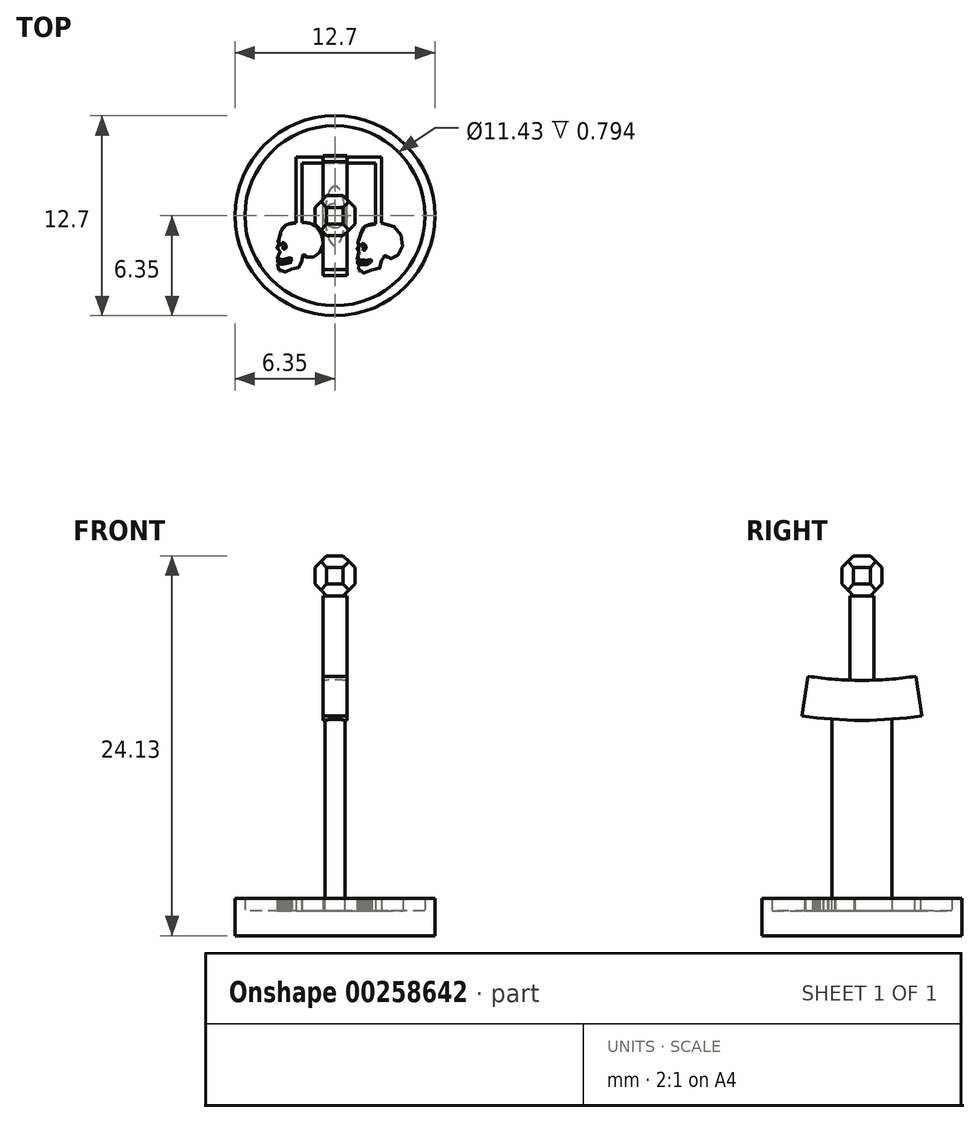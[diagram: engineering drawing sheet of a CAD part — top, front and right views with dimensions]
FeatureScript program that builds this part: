
annotation { "Feature Type Name" : "Feature", "Feature Type Description" : "" }
export const myFeature = defineFeature(function(context is Context, id is Id, definition is map)
    precondition{}
    {
        {
            var Q0;
            Q0=qCreatedBy(makeId("Top.planeOp"),FACE);
            var sketch = newSketch(context, id + "F0", { "sketchPlane" : qUnion([Q0])});
            skCircle(sketch, "E0", {"center": v(0, 0) * mm, "radius": 6.35 * mm});
            skSolve(sketch);
        }
        {
            var Q0;
            Q0 = qSketchRegion(id + "F0", true);
            extrude(context, id + "F1", {"entities" : qUnion([Q0]), "depth" : 1.59 * mm});
        }
        {
            var Q0;
            Q0=makeQuery(id+"F1.opExtrude","CAP_FACE",FACE,{"disambiguationData":[OSD([sQuery(id+"F0.wireOp",EDGE,"E0")])],"isStart":false});
            var sketch = newSketch(context, id + "F2", { "sketchPlane" : qUnion([Q0])});
            skCircle(sketch, "E1", {"center": v(0, 0) * mm, "radius": 5.72 * mm});
            skCircle(sketch, "E2.0", {"center": v(0, 0) * mm, "radius": 6.35 * mm});
            skFitSpline(sketch, "E3", {"points": [v(-2.99, -3.48) * mm, v(-2.95, -3.46) * mm, v(-2.86, -3.42) * mm, v(-2.74, -3.39) * mm, v(-2.6, -3.35) * mm, v(-2.43, -3.3) * mm, v(-2.3, -3.28) * mm, v(-2.2, -3.25) * mm, v(-2.15, -3.14) * mm, v(-2.13, -3.01) * mm, v(-2.13, -2.82) * mm, v(-2.12, -2.72) * mm, v(-2.07, -2.57) * mm, v(-2, -2.44) * mm, v(-1.95, -2.43) * mm, v(-1.87, -2.47) * mm, v(-1.8, -2.57) * mm, v(-1.76, -2.65) * mm, v(-1.67, -2.67) * mm, v(-1.54, -2.67) * mm, v(-1.4, -2.63) * mm, v(-1.28, -2.57) * mm, v(-1.17, -2.5) * mm, v(-1.04, -2.4) * mm, v(-0.91, -2.23) * mm, v(-0.83, -2.05) * mm, v(-0.77, -1.87) * mm, v(-0.77, -1.6) * mm, v(-0.82, -1.35) * mm, v(-0.9, -1.14) * mm, v(-1.03, -0.9) * mm, v(-1.19, -0.72) * mm, v(-1.49, -0.53) * mm, v(-1.79, -0.45) * mm, v(-2.09, -0.45) * mm, v(-2.47, -0.46) * mm, v(-2.74, -0.46) * mm, v(-2.94, -0.5) * mm, v(-3.18, -0.62) * mm, v(-3.33, -0.78) * mm, v(-3.4, -0.96) * mm, v(-3.45, -1.13) * mm, v(-3.45, -1.23) * mm, v(-3.5, -1.37) * mm, v(-3.57, -1.5) * mm, v(-3.61, -1.59) * mm, v(-3.6, -1.65) * mm, v(-3.56, -1.72) * mm, v(-3.53, -1.77) * mm, v(-3.51, -1.85) * mm, v(-3.57, -1.93) * mm, v(-3.6, -1.96) * mm, v(-3.66, -2) * mm, v(-3.66, -2.01) * mm, v(-3.67, -2.03) * mm, v(-3.66, -2.05) * mm, v(-3.65, -2.07) * mm, v(-3.63, -2.09) * mm, v(-3.53, -2.23) * mm, v(-3.46, -2.33) * mm, v(-3.48, -2.4) * mm, v(-3.54, -2.44) * mm, v(-3.6, -2.48) * mm, v(-3.61, -2.49) * mm, v(-3.6, -2.5) * mm, v(-3.57, -2.52) * mm, v(-3.56, -2.54) * mm, v(-3.57, -2.57) * mm, v(-3.6, -2.6) * mm, v(-3.65, -2.66) * mm, v(-3.66, -2.72) * mm, v(-3.59, -2.76) * mm, v(-3.44, -2.8) * mm, v(-3.3, -2.78) * mm, v(-3.16, -2.74) * mm, v(-3.02, -2.7) * mm, v(-2.86, -2.69) * mm, v(-2.77, -2.7) * mm, v(-2.74, -2.74) * mm, v(-2.73, -2.81) * mm, v(-2.74, -2.88) * mm, v(-2.78, -2.96) * mm, v(-2.92, -3) * mm, v(-3, -3.03) * mm, v(-3.1, -3.05) * mm, v(-3.29, -3.07) * mm, v(-3.43, -3.07) * mm, v(-3.55, -3.04) * mm, v(-3.62, -3.03) * mm, v(-3.64, -3.06) * mm, v(-3.59, -3.13) * mm, v(-3.56, -3.22) * mm, v(-3.58, -3.3) * mm, v(-3.6, -3.39) * mm, v(-3.6, -3.5) * mm, v(-3.52, -3.56) * mm, v(-3.18, -3.57) * mm, v(-2.99, -3.48) * mm]});
            skFitSpline(sketch, "E4", {"points": [v(-3.38, -1.71) * mm, v(-3.39, -1.8) * mm, v(-3.34, -1.88) * mm, v(-3.3, -1.95) * mm, v(-3.3, -2.01) * mm, v(-3.3, -2.06) * mm, v(-3.26, -2.12) * mm, v(-3.17, -2.1) * mm, v(-3.11, -2) * mm, v(-3.11, -1.92) * mm, v(-3.13, -1.84) * mm, v(-3.19, -1.76) * mm, v(-3.25, -1.72) * mm, v(-3.32, -1.7) * mm, v(-3.38, -1.71) * mm]});
            skLineSegment(sketch, "E5", {"start": v(-3.52, -2.83) * mm, "end": v(-3.52, -2.9) * mm});
            skLineSegment(sketch, "E6", {"start": v(-3.52, -2.9) * mm, "end": v(-3.44, -2.92) * mm});
            skLineSegment(sketch, "E7", {"start": v(-3.44, -2.92) * mm, "end": v(-3.44, -2.85) * mm});
            skLineSegment(sketch, "E8", {"start": v(-3.44, -2.85) * mm, "end": v(-3.52, -2.83) * mm});
            skLineSegment(sketch, "E9", {"start": v(-3.41, -2.85) * mm, "end": v(-3.41, -2.92) * mm});
            skLineSegment(sketch, "E10", {"start": v(-3.41, -2.92) * mm, "end": v(-3.33, -2.92) * mm});
            skLineSegment(sketch, "E11", {"start": v(-3.33, -2.92) * mm, "end": v(-3.33, -2.85) * mm});
            skLineSegment(sketch, "E12", {"start": v(-3.33, -2.85) * mm, "end": v(-3.41, -2.85) * mm});
            skLineSegment(sketch, "E13", {"start": v(-3.3, -2.85) * mm, "end": v(-3.3, -2.92) * mm});
            skLineSegment(sketch, "E14", {"start": v(-3.3, -2.92) * mm, "end": v(-3.22, -2.92) * mm});
            skLineSegment(sketch, "E15", {"start": v(-3.22, -2.92) * mm, "end": v(-3.23, -2.84) * mm});
            skLineSegment(sketch, "E16", {"start": v(-3.23, -2.84) * mm, "end": v(-3.3, -2.85) * mm});
            skLineSegment(sketch, "E17", {"start": v(-3.2, -2.83) * mm, "end": v(-3.2, -2.92) * mm});
            skLineSegment(sketch, "E18", {"start": v(-3.2, -2.92) * mm, "end": v(-3.12, -2.9) * mm});
            skLineSegment(sketch, "E19", {"start": v(-3.12, -2.9) * mm, "end": v(-3.12, -2.81) * mm});
            skLineSegment(sketch, "E20", {"start": v(-3.12, -2.81) * mm, "end": v(-3.2, -2.83) * mm});
            skLineSegment(sketch, "E21", {"start": v(-3.09, -2.8) * mm, "end": v(-3.09, -2.9) * mm});
            skLineSegment(sketch, "E22", {"start": v(-3.09, -2.9) * mm, "end": v(-3, -2.87) * mm});
            skLineSegment(sketch, "E23", {"start": v(-3, -2.87) * mm, "end": v(-3, -2.77) * mm});
            skLineSegment(sketch, "E24", {"start": v(-3, -2.77) * mm, "end": v(-3.09, -2.8) * mm});
            skLineSegment(sketch, "E25", {"start": v(-2.98, -2.75) * mm, "end": v(-2.98, -2.86) * mm});
            skLineSegment(sketch, "E26", {"start": v(-2.98, -2.86) * mm, "end": v(-2.9, -2.83) * mm});
            skLineSegment(sketch, "E27", {"start": v(-2.9, -2.83) * mm, "end": v(-2.9, -2.73) * mm});
            skLineSegment(sketch, "E28", {"start": v(-2.9, -2.73) * mm, "end": v(-2.98, -2.75) * mm});
            skLineSegment(sketch, "E29", {"start": v(-2.87, -2.72) * mm, "end": v(-2.87, -2.81) * mm});
            skLineSegment(sketch, "E30", {"start": v(-2.87, -2.81) * mm, "end": v(-2.77, -2.77) * mm});
            skLineSegment(sketch, "E31", {"start": v(-2.77, -2.8) * mm, "end": v(-2.88, -2.85) * mm});
            skLineSegment(sketch, "E32", {"start": v(-2.88, -2.85) * mm, "end": v(-2.88, -2.94) * mm});
            skLineSegment(sketch, "E33", {"start": v(-2.9, -2.95) * mm, "end": v(-2.9, -2.87) * mm});
            skLineSegment(sketch, "E34", {"start": v(-2.9, -2.87) * mm, "end": v(-2.98, -2.9) * mm});
            skLineSegment(sketch, "E35", {"start": v(-2.98, -2.9) * mm, "end": v(-2.98, -2.97) * mm});
            skLineSegment(sketch, "E36", {"start": v(-2.98, -2.97) * mm, "end": v(-2.9, -2.95) * mm});
            skLineSegment(sketch, "E37", {"start": v(-3, -2.9) * mm, "end": v(-3.09, -2.92) * mm});
            skPoint(sketch, "E37.startSnap0", {"position": v(-3.16, -2.9) * mm});
            skLineSegment(sketch, "E38", {"start": v(-3.09, -2.92) * mm, "end": v(-3.09, -3) * mm});
            skLineSegment(sketch, "E39", {"start": v(-3.09, -3) * mm, "end": v(-3, -2.98) * mm});
            skLineSegment(sketch, "E40", {"start": v(-3, -2.98) * mm, "end": v(-3, -2.9) * mm});
            skLineSegment(sketch, "E41", {"start": v(-3.12, -2.94) * mm, "end": v(-3.2, -2.95) * mm});
            skLineSegment(sketch, "E42", {"start": v(-3.2, -2.95) * mm, "end": v(-3.2, -3.02) * mm});
            skLineSegment(sketch, "E43", {"start": v(-3.2, -3.02) * mm, "end": v(-3.12, -3.01) * mm});
            skLineSegment(sketch, "E44", {"start": v(-3.12, -3.01) * mm, "end": v(-3.12, -2.94) * mm});
            skLineSegment(sketch, "E45", {"start": v(-3.23, -2.95) * mm, "end": v(-3.3, -2.95) * mm});
            skLineSegment(sketch, "E46", {"start": v(-3.3, -2.95) * mm, "end": v(-3.3, -3.03) * mm});
            skLineSegment(sketch, "E47", {"start": v(-3.3, -3.03) * mm, "end": v(-3.23, -3.03) * mm});
            skLineSegment(sketch, "E48", {"start": v(-3.23, -3.03) * mm, "end": v(-3.23, -2.95) * mm});
            skLineSegment(sketch, "E49", {"start": v(-3.33, -2.95) * mm, "end": v(-3.41, -2.95) * mm});
            skLineSegment(sketch, "E50", {"start": v(-3.41, -2.95) * mm, "end": v(-3.41, -3.02) * mm});
            skLineSegment(sketch, "E51", {"start": v(-3.41, -3.02) * mm, "end": v(-3.33, -3.03) * mm});
            skLineSegment(sketch, "E52", {"start": v(-3.33, -3.03) * mm, "end": v(-3.33, -2.95) * mm});
            skLineSegment(sketch, "E53", {"start": v(-3.52, -2.94) * mm, "end": v(-3.44, -2.95) * mm});
            skLineSegment(sketch, "E54", {"start": v(-3.44, -2.95) * mm, "end": v(-3.44, -3.01) * mm});
            skLineSegment(sketch, "E55", {"start": v(-3.44, -3.01) * mm, "end": v(-3.52, -3) * mm});
            skLineSegment(sketch, "E56", {"start": v(-3.52, -3) * mm, "end": v(-3.52, -2.94) * mm});
            skLineSegment(sketch, "E57", {"start": v(-3.64, -2.91) * mm, "end": v(-3.55, -2.94) * mm});
            skLineSegment(sketch, "E58", {"start": v(-3.55, -2.94) * mm, "end": v(-3.55, -3) * mm});
            skLineSegment(sketch, "E59", {"start": v(-3.55, -2.82) * mm, "end": v(-3.55, -2.9) * mm});
            skLineSegment(sketch, "E60", {"start": v(-3.55, -2.9) * mm, "end": v(-3.64, -2.88) * mm});
            skArc(sketch, "E61", {"start": v(-3.55, -2.82) * mm, "mid": v(-3.61, -2.82) * mm, "end": v(-3.64, -2.88) * mm});
            skArc(sketch, "E62", {"start": v(-3.64, -2.91) * mm, "mid": v(-3.61, -2.97) * mm, "end": v(-3.55, -3) * mm});
            skArc(sketch, "E63", {"start": v(-2.77, -2.77) * mm, "mid": v(-2.82, -2.73) * mm, "end": v(-2.87, -2.72) * mm});
            skArc(sketch, "E64", {"start": v(-2.88, -2.94) * mm, "mid": v(-2.8, -2.9) * mm, "end": v(-2.77, -2.8) * mm});
            skFitSpline(sketch, "E65", {"points": [v(2.09, -3.54) * mm, v(2.12, -3.52) * mm, v(2.21, -3.48) * mm, v(2.33, -3.45) * mm, v(2.46, -3.4) * mm, v(2.64, -3.36) * mm, v(2.76, -3.34) * mm, v(2.87, -3.3) * mm, v(2.92, -3.2) * mm, v(2.94, -3.08) * mm, v(2.95, -2.88) * mm, v(2.95, -2.78) * mm, v(3, -2.63) * mm, v(3.08, -2.5) * mm, v(3.13, -2.5) * mm, v(3.2, -2.53) * mm, v(3.27, -2.64) * mm, v(3.31, -2.71) * mm, v(3.4, -2.74) * mm, v(3.53, -2.74) * mm, v(3.67, -2.69) * mm, v(3.8, -2.63) * mm, v(3.9, -2.56) * mm, v(4.03, -2.46) * mm, v(4.16, -2.29) * mm, v(4.24, -2.1) * mm, v(4.3, -1.94) * mm, v(4.3, -1.66) * mm, v(4.25, -1.41) * mm, v(4.18, -1.2) * mm, v(4.04, -0.96) * mm, v(3.89, -0.78) * mm, v(3.58, -0.6) * mm, v(3.29, -0.51) * mm, v(2.97, -0.48) * mm, v(2.59, -0.52) * mm, v(2.33, -0.52) * mm, v(2.13, -0.57) * mm, v(1.9, -0.68) * mm, v(1.74, -0.84) * mm, v(1.67, -1.02) * mm, v(1.62, -1.2) * mm, v(1.63, -1.3) * mm, v(1.57, -1.43) * mm, v(1.5, -1.57) * mm, v(1.46, -1.65) * mm, v(1.46, -1.71) * mm, v(1.51, -1.78) * mm, v(1.54, -1.83) * mm, v(1.56, -1.91) * mm, v(1.5, -1.99) * mm, v(1.46, -2.02) * mm, v(1.41, -2.06) * mm, v(1.4, -2.08) * mm, v(1.4, -2.1) * mm, v(1.4, -2.11) * mm, v(1.42, -2.13) * mm, v(1.44, -2.15) * mm, v(1.54, -2.3) * mm, v(1.61, -2.4) * mm, v(1.6, -2.46) * mm, v(1.53, -2.5) * mm, v(1.47, -2.54) * mm, v(1.46, -2.55) * mm, v(1.48, -2.56) * mm, v(1.5, -2.58) * mm, v(1.52, -2.6) * mm, v(1.5, -2.63) * mm, v(1.47, -2.67) * mm, v(1.43, -2.72) * mm, v(1.41, -2.78) * mm, v(1.49, -2.82) * mm, v(1.63, -2.85) * mm, v(1.77, -2.85) * mm, v(1.91, -2.8) * mm, v(2.05, -2.77) * mm, v(2.21, -2.75) * mm, v(2.3, -2.77) * mm, v(2.33, -2.8) * mm, v(2.35, -2.88) * mm, v(2.33, -2.95) * mm, v(2.29, -3.02) * mm, v(2.15, -3.07) * mm, v(2.07, -3.09) * mm, v(1.97, -3.11) * mm, v(1.79, -3.14) * mm, v(1.64, -3.13) * mm, v(1.52, -3.1) * mm, v(1.45, -3.1) * mm, v(1.43, -3.13) * mm, v(1.48, -3.2) * mm, v(1.51, -3.28) * mm, v(1.5, -3.36) * mm, v(1.48, -3.45) * mm, v(1.48, -3.56) * mm, v(1.55, -3.62) * mm, v(1.9, -3.63) * mm, v(2.09, -3.54) * mm]});
            skFitSpline(sketch, "E66", {"points": [v(1.7, -1.77) * mm, v(1.69, -1.86) * mm, v(1.73, -1.95) * mm, v(1.78, -2) * mm, v(1.78, -2.08) * mm, v(1.76, -2.13) * mm, v(1.8, -2.19) * mm, v(1.9, -2.17) * mm, v(1.96, -2.07) * mm, v(1.96, -1.98) * mm, v(1.95, -1.9) * mm, v(1.88, -1.82) * mm, v(1.82, -1.78) * mm, v(1.75, -1.76) * mm, v(1.7, -1.77) * mm]});
            skLineSegment(sketch, "E67", {"start": v(1.55, -2.9) * mm, "end": v(1.55, -2.97) * mm});
            skLineSegment(sketch, "E68", {"start": v(1.55, -2.97) * mm, "end": v(1.63, -2.98) * mm});
            skLineSegment(sketch, "E69", {"start": v(1.63, -2.98) * mm, "end": v(1.63, -2.9) * mm});
            skLineSegment(sketch, "E70", {"start": v(1.63, -2.9) * mm, "end": v(1.55, -2.9) * mm});
            skLineSegment(sketch, "E71", {"start": v(1.66, -2.91) * mm, "end": v(1.66, -2.98) * mm});
            skLineSegment(sketch, "E72", {"start": v(1.66, -2.98) * mm, "end": v(1.74, -2.98) * mm});
            skLineSegment(sketch, "E73", {"start": v(1.74, -2.98) * mm, "end": v(1.74, -2.92) * mm});
            skLineSegment(sketch, "E74", {"start": v(1.74, -2.92) * mm, "end": v(1.66, -2.91) * mm});
            skLineSegment(sketch, "E75", {"start": v(1.77, -2.91) * mm, "end": v(1.77, -2.98) * mm});
            skLineSegment(sketch, "E76", {"start": v(1.77, -2.98) * mm, "end": v(1.85, -2.98) * mm});
            skLineSegment(sketch, "E77", {"start": v(1.85, -2.98) * mm, "end": v(1.85, -2.9) * mm});
            skLineSegment(sketch, "E78", {"start": v(1.85, -2.9) * mm, "end": v(1.77, -2.91) * mm});
            skLineSegment(sketch, "E79", {"start": v(1.88, -2.9) * mm, "end": v(1.88, -2.98) * mm});
            skLineSegment(sketch, "E80", {"start": v(1.88, -2.98) * mm, "end": v(1.95, -2.96) * mm});
            skLineSegment(sketch, "E81", {"start": v(1.95, -2.96) * mm, "end": v(1.95, -2.88) * mm});
            skLineSegment(sketch, "E82", {"start": v(1.95, -2.88) * mm, "end": v(1.88, -2.9) * mm});
            skLineSegment(sketch, "E83", {"start": v(1.99, -2.86) * mm, "end": v(1.99, -2.96) * mm});
            skLineSegment(sketch, "E84", {"start": v(1.99, -2.96) * mm, "end": v(2.07, -2.93) * mm});
            skLineSegment(sketch, "E85", {"start": v(2.07, -2.93) * mm, "end": v(2.07, -2.83) * mm});
            skLineSegment(sketch, "E86", {"start": v(2.07, -2.83) * mm, "end": v(1.99, -2.86) * mm});
            skLineSegment(sketch, "E87", {"start": v(2.1, -2.82) * mm, "end": v(2.1, -2.92) * mm});
            skLineSegment(sketch, "E88", {"start": v(2.1, -2.92) * mm, "end": v(2.17, -2.9) * mm});
            skLineSegment(sketch, "E89", {"start": v(2.17, -2.9) * mm, "end": v(2.17, -2.8) * mm});
            skLineSegment(sketch, "E90", {"start": v(2.17, -2.8) * mm, "end": v(2.1, -2.82) * mm});
            skLineSegment(sketch, "E91", {"start": v(2.2, -2.79) * mm, "end": v(2.2, -2.88) * mm});
            skLineSegment(sketch, "E92", {"start": v(2.2, -2.88) * mm, "end": v(2.3, -2.84) * mm});
            skLineSegment(sketch, "E93", {"start": v(2.3, -2.87) * mm, "end": v(2.2, -2.92) * mm});
            skLineSegment(sketch, "E94", {"start": v(2.2, -2.92) * mm, "end": v(2.2, -3) * mm});
            skLineSegment(sketch, "E95", {"start": v(2.17, -3.01) * mm, "end": v(2.17, -2.93) * mm});
            skLineSegment(sketch, "E96", {"start": v(2.17, -2.93) * mm, "end": v(2.1, -2.96) * mm});
            skLineSegment(sketch, "E97", {"start": v(2.1, -2.96) * mm, "end": v(2.1, -3.04) * mm});
            skLineSegment(sketch, "E98", {"start": v(2.1, -3.04) * mm, "end": v(2.17, -3.01) * mm});
            skLineSegment(sketch, "E99", {"start": v(2.06, -2.97) * mm, "end": v(1.98, -2.99) * mm});
            skPoint(sketch, "E99.startSnap0", {"position": v(1.91, -2.97) * mm});
            skLineSegment(sketch, "E100", {"start": v(1.98, -2.99) * mm, "end": v(1.99, -3.07) * mm});
            skLineSegment(sketch, "E101", {"start": v(1.99, -3.07) * mm, "end": v(2.07, -3.05) * mm});
            skLineSegment(sketch, "E102", {"start": v(2.07, -3.05) * mm, "end": v(2.06, -2.97) * mm});
            skLineSegment(sketch, "E103", {"start": v(1.95, -3) * mm, "end": v(1.88, -3.01) * mm});
            skLineSegment(sketch, "E104", {"start": v(1.88, -3.01) * mm, "end": v(1.88, -3.09) * mm});
            skLineSegment(sketch, "E105", {"start": v(1.88, -3.09) * mm, "end": v(1.95, -3.07) * mm});
            skLineSegment(sketch, "E106", {"start": v(1.95, -3.07) * mm, "end": v(1.95, -3) * mm});
            skLineSegment(sketch, "E107", {"start": v(1.84, -3.02) * mm, "end": v(1.77, -3.02) * mm});
            skLineSegment(sketch, "E108", {"start": v(1.77, -3.02) * mm, "end": v(1.77, -3.1) * mm});
            skLineSegment(sketch, "E109", {"start": v(1.77, -3.1) * mm, "end": v(1.85, -3.1) * mm});
            skLineSegment(sketch, "E110", {"start": v(1.85, -3.1) * mm, "end": v(1.84, -3.02) * mm});
            skLineSegment(sketch, "E111", {"start": v(1.74, -3.02) * mm, "end": v(1.66, -3.02) * mm});
            skLineSegment(sketch, "E112", {"start": v(1.66, -3.02) * mm, "end": v(1.66, -3.08) * mm});
            skLineSegment(sketch, "E113", {"start": v(1.66, -3.08) * mm, "end": v(1.74, -3.1) * mm});
            skLineSegment(sketch, "E114", {"start": v(1.74, -3.1) * mm, "end": v(1.74, -3.02) * mm});
            skLineSegment(sketch, "E115", {"start": v(1.56, -3) * mm, "end": v(1.63, -3.01) * mm});
            skLineSegment(sketch, "E116", {"start": v(1.63, -3.01) * mm, "end": v(1.63, -3.08) * mm});
            skLineSegment(sketch, "E117", {"start": v(1.63, -3.08) * mm, "end": v(1.55, -3.07) * mm});
            skLineSegment(sketch, "E118", {"start": v(1.55, -3.07) * mm, "end": v(1.56, -3) * mm});
            skLineSegment(sketch, "E119", {"start": v(1.43, -2.97) * mm, "end": v(1.52, -3) * mm});
            skLineSegment(sketch, "E120", {"start": v(1.52, -3) * mm, "end": v(1.52, -3.06) * mm});
            skLineSegment(sketch, "E121", {"start": v(1.52, -2.89) * mm, "end": v(1.52, -2.96) * mm});
            skLineSegment(sketch, "E122", {"start": v(1.52, -2.96) * mm, "end": v(1.43, -2.94) * mm});
            skArc(sketch, "E123", {"start": v(1.52, -2.89) * mm, "mid": v(1.46, -2.88) * mm, "end": v(1.43, -2.94) * mm});
            skArc(sketch, "E124", {"start": v(1.43, -2.97) * mm, "mid": v(1.46, -3.04) * mm, "end": v(1.52, -3.06) * mm});
            skArc(sketch, "E125", {"start": v(2.3, -2.84) * mm, "mid": v(2.26, -2.8) * mm, "end": v(2.2, -2.79) * mm});
            skArc(sketch, "E126", {"start": v(2.2, -3) * mm, "mid": v(2.27, -2.95) * mm, "end": v(2.3, -2.87) * mm});
            skLineSegment(sketch, "E127", {"start": v(-2.47, -0.46) * mm, "end": v(-2.47, 3.73) * mm});
            skLineSegment(sketch, "E128", {"start": v(-2.47, 3.73) * mm, "end": v(2.97, 3.73) * mm});
            skLineSegment(sketch, "E129", {"start": v(2.97, 3.73) * mm, "end": v(2.97, -0.48) * mm});
            skLineSegment(sketch, "E130", {"start": v(-2.09, -0.45) * mm, "end": v(-2.09, 3.35) * mm});
            skLineSegment(sketch, "E131", {"start": v(-2.09, 3.35) * mm, "end": v(2.59, 3.35) * mm});
            skLineSegment(sketch, "E132", {"start": v(2.59, 3.35) * mm, "end": v(2.59, -0.52) * mm});
            skSolve(sketch);
        }
        {
            var Q0;
            Q0 = qSketchRegion(id + "F2", true);
            var Q1;
            Q1=makeQuery(id+"F2.imprint","IMPRINT",FACE,{"disambiguationData":[TD([[makeQuery(id+"F2.imprint","IMPRINT",EDGE,{"derivedFrom":sQuery(id+"F2.wireOp",EDGE,"8ff43451-18cf-4e1d-a6c1-207112ed4b83")}),-1.0]])]});
            var Q2;
            {var subQ0=sQuery(id+"F2.wireOp",EDGE,"f0ZndoA6-M2V5-AV1c-evuh-kt5lGmkfnjif");Q2=makeQuery(id+"F2.imprint","IMPRINT",FACE,{"disambiguationData":[TD([[makeQuery(id+"F2.imprint","IMPRINT",EDGE,{"derivedFrom":subQ0}),-1.0]])]});}
            var Q3;
            Q3=makeQuery(id+"F2.imprint","IMPRINT",FACE,{"disambiguationData":[TD([[makeQuery(id+"F2.imprint","IMPRINT",EDGE,{"derivedFrom":sQuery(id+"F2.wireOp",EDGE,"9676f148-d3db-47f1-8d18-ed8e72a81f72")}),-1.0]])]});
            var Q4;
            Q4=makeQuery(id+"F2.imprint","IMPRINT",FACE,{"disambiguationData":[TD([[makeQuery(id+"F2.imprint","IMPRINT",EDGE,{"derivedFrom":sQuery(id+"F2.wireOp",EDGE,"6HFhc678-r75o-y9sA-huqe-qlUwMVaPKWuP")}),-1.0]])]});
            var Q5;
            Q5=makeQuery(id+"F2.imprint","IMPRINT",FACE,{"disambiguationData":[TD([[makeQuery(id+"F2.imprint","IMPRINT",EDGE,{"derivedFrom":sQuery(id+"F2.wireOp",EDGE,"Xs92rVgm-BZGN-NsKB-OARH-R7qVRdKGH7H2")}),-1.0]])]});
            var Q6;
            Q6=makeQuery(id+"F2.imprint","IMPRINT",FACE,{"disambiguationData":[TD([[makeQuery(id+"F2.imprint","IMPRINT",EDGE,{"derivedFrom":sQuery(id+"F2.wireOp",EDGE,"E6WdCPIx-waOx-idA0-XJ1L-eRR6RgLmtCCS")}),-1.0]])]});
            var Q7;
            Q7=makeQuery(id+"F2.imprint","IMPRINT",FACE,{"disambiguationData":[TD([[makeQuery(id+"F2.imprint","IMPRINT",EDGE,{"derivedFrom":sQuery(id+"F2.wireOp",EDGE,"k1KiTlt2-ZZcU-dbgL-0rmk-Dgw59MTWpoCj")}),1.0]])]});
            var Q8;
            Q8=makeQuery(id+"F2.imprint","IMPRINT",FACE,{"disambiguationData":[TD([[makeQuery(id+"F2.imprint","IMPRINT",EDGE,{"derivedFrom":sQuery(id+"F2.wireOp",EDGE,"Z35Rb9R9-Rahv-nOh3-XL17-nKowExZUsZCT")}),1.0]])]});
            var Q9;
            Q9=makeQuery(id+"F2.imprint","IMPRINT",FACE,{"disambiguationData":[TD([[makeQuery(id+"F2.imprint","IMPRINT",EDGE,{"derivedFrom":sQuery(id+"F2.wireOp",EDGE,"Qg5ONqqo-2bfa-kxUG-9bmz-Wc6T9dYv9u8v")}),1.0]])]});
            var Q10;
            Q10=makeQuery(id+"F2.imprint","IMPRINT",FACE,{"disambiguationData":[TD([[makeQuery(id+"F2.imprint","IMPRINT",EDGE,{"derivedFrom":sQuery(id+"F2.wireOp",EDGE,"AjI9mxPJ-XULu-6nMp-z6qf-DJC3dJrP3SV3")}),1.0]])]});
            var Q11;
            Q11=makeQuery(id+"F2.imprint","IMPRINT",FACE,{"disambiguationData":[TD([[makeQuery(id+"F2.imprint","IMPRINT",EDGE,{"derivedFrom":sQuery(id+"F2.wireOp",EDGE,"SVXRag1M-qj8O-Xghp-BRg2-clQjxRkFYdgi")}),1.0]])]});
            var Q12;
            Q12=makeQuery(id+"F2.imprint","IMPRINT",FACE,{"disambiguationData":[TD([[makeQuery(id+"F2.imprint","IMPRINT",EDGE,{"derivedFrom":sQuery(id+"F2.wireOp",EDGE,"QknCvVvT-fZar-JZdj-N9ht-K5PjY9N2CpLl")}),1.0]])]});
            var Q13;
            Q13=makeQuery(id+"F2.imprint","IMPRINT",FACE,{"disambiguationData":[TD([[makeQuery(id+"F2.imprint","IMPRINT",EDGE,{"derivedFrom":sQuery(id+"F2.wireOp",EDGE,"IwH12iTC-POgW-ZuDk-O3qY-x9Lpsw7XAAf3")}),1.0]])]});
            var Q14;
            Q14=makeQuery(id+"F2.imprint","IMPRINT",FACE,{"disambiguationData":[TD([[makeQuery(id+"F2.imprint","IMPRINT",EDGE,{"derivedFrom":sQuery(id+"F2.wireOp",EDGE,"UGZWNjaC-YJYr-0zUO-1gu3-YYbdkgLbKj1s")}),1.0]])]});
            var Q15;
            Q15=makeQuery(id+"F2.imprint","IMPRINT",FACE,{"disambiguationData":[TD([[makeQuery(id+"F2.imprint","IMPRINT",EDGE,{"derivedFrom":sQuery(id+"F2.wireOp",EDGE,"faBvcXIA-NgVa-Zogo-Hth3-byswulnYsCry")}),1.0]])]});
            var Q16;
            Q16=makeQuery(id+"F2.imprint","IMPRINT",FACE,{"disambiguationData":[TD([[makeQuery(id+"F2.imprint","IMPRINT",EDGE,{"derivedFrom":sQuery(id+"F2.wireOp",EDGE,"z3QF5KZu-mklS-Cyfl-OEiK-EEmoJCKWUvB4")}),1.0]])]});
            var Q17;
            Q17=makeQuery(id+"F2.imprint","IMPRINT",FACE,{"disambiguationData":[TD([[makeQuery(id+"F2.imprint","IMPRINT",EDGE,{"derivedFrom":sQuery(id+"F2.wireOp",EDGE,"V2NIJvH9-TtMw-qc9R-an5m-Kvf6aCU9D1Wj")}),1.0]])]});
            var Q18;
            Q18=makeQuery(id+"F2.imprint","IMPRINT",FACE,{"disambiguationData":[TD([[makeQuery(id+"F2.imprint","IMPRINT",EDGE,{"derivedFrom":sQuery(id+"F2.wireOp",EDGE,"QeDBAyft-zymL-5vx5-wYYY-tHA32UShdvIB")}),1.0]])]});
            var Q19;
            Q19=makeQuery(id+"F2.imprint","IMPRINT",FACE,{"disambiguationData":[TD([[makeQuery(id+"F2.imprint","IMPRINT",EDGE,{"derivedFrom":sQuery(id+"F2.wireOp",EDGE,"WRGg1PvO-WrmP-NIcv-oRJx-bzyG9trbOkE2")}),1.0]])]});
            var Q20;
            Q20=makeQuery(id+"F2.imprint","IMPRINT",FACE,{"disambiguationData":[TD([[makeQuery(id+"F2.imprint","IMPRINT",EDGE,{"derivedFrom":sQuery(id+"F2.wireOp",EDGE,"75ec5599-b41b-4d6a-bb06-b73393bb844d")}),-1.0]])]});
            var Q21;
            Q21=makeQuery(id+"F2.imprint","IMPRINT",FACE,{"disambiguationData":[TD([[makeQuery(id+"F2.imprint","IMPRINT",EDGE,{"derivedFrom":sQuery(id+"F2.wireOp",EDGE,"62e6d997-3ff5-4a1c-8de8-b05959ec7cbc")}),-1.0]])]});
            var Q22;
            Q22=makeQuery(id+"F2.imprint","IMPRINT",FACE,{"disambiguationData":[TD([[makeQuery(id+"F2.imprint","IMPRINT",EDGE,{"derivedFrom":sQuery(id+"F2.wireOp",EDGE,"b8f4918c-dbd8-4fdd-af15-bc96a6b6a90d")}),-1.0]])]});
            var Q23;
            Q23=makeQuery(id+"F2.imprint","IMPRINT",FACE,{"disambiguationData":[TD([[makeQuery(id+"F2.imprint","IMPRINT",EDGE,{"derivedFrom":sQuery(id+"F2.wireOp",EDGE,"337819dd-2963-4144-94d7-e260421f4e37")}),1.0]])]});
            var Q24;
            Q24=makeQuery(id+"F2.imprint","IMPRINT",FACE,{"disambiguationData":[TD([[makeQuery(id+"F2.imprint","IMPRINT",EDGE,{"derivedFrom":sQuery(id+"F2.wireOp",EDGE,"19c6ec17-bb67-46df-91db-361c1b9a8fc6")}),1.0]])]});
            var Q25;
            Q25=makeQuery(id+"F2.imprint","IMPRINT",FACE,{"disambiguationData":[TD([[makeQuery(id+"F2.imprint","IMPRINT",EDGE,{"derivedFrom":sQuery(id+"F2.wireOp",EDGE,"b55352ad-c42c-4425-987b-4bb80f046402")}),1.0]])]});
            var Q26;
            Q26=makeQuery(id+"F2.imprint","IMPRINT",FACE,{"disambiguationData":[TD([[makeQuery(id+"F2.imprint","IMPRINT",EDGE,{"derivedFrom":sQuery(id+"F2.wireOp",EDGE,"b27b330e-c63e-4a5d-9a41-1e5f11f57855")}),1.0]])]});
            var Q27;
            Q27=makeQuery(id+"F2.imprint","IMPRINT",FACE,{"disambiguationData":[TD([[makeQuery(id+"F2.imprint","IMPRINT",EDGE,{"derivedFrom":sQuery(id+"F2.wireOp",EDGE,"cd0931f7-213e-4ee0-afb0-8455a1d6fb19")}),1.0]])]});
            var Q28;
            Q28=makeQuery(id+"F2.imprint","IMPRINT",FACE,{"disambiguationData":[TD([[makeQuery(id+"F2.imprint","IMPRINT",EDGE,{"derivedFrom":sQuery(id+"F2.wireOp",EDGE,"2ee7f471-c0e9-471b-9897-f54198c6bebe")}),1.0]])]});
            var Q29;
            Q29=makeQuery(id+"F2.imprint","IMPRINT",FACE,{"disambiguationData":[TD([[makeQuery(id+"F2.imprint","IMPRINT",EDGE,{"derivedFrom":sQuery(id+"F2.wireOp",EDGE,"1a649881-7116-4bcf-9e85-0b71573aa8aa")}),1.0]])]});
            var Q30;
            Q30=makeQuery(id+"F2.imprint","IMPRINT",FACE,{"disambiguationData":[TD([[makeQuery(id+"F2.imprint","IMPRINT",EDGE,{"derivedFrom":sQuery(id+"F2.wireOp",EDGE,"c0ec6f99-1aba-4aca-9953-efef360278b0")}),1.0]])]});
            var Q31;
            Q31=makeQuery(id+"F2.imprint","IMPRINT",FACE,{"disambiguationData":[TD([[makeQuery(id+"F2.imprint","IMPRINT",EDGE,{"derivedFrom":sQuery(id+"F2.wireOp",EDGE,"17c59965-fe3a-40f4-ab79-7e7308dcb645")}),1.0]])]});
            var Q32;
            Q32=makeQuery(id+"F2.imprint","IMPRINT",FACE,{"disambiguationData":[TD([[makeQuery(id+"F2.imprint","IMPRINT",EDGE,{"derivedFrom":sQuery(id+"F2.wireOp",EDGE,"bf3a8e90-f25c-4be5-acd2-482a28ec085b")}),1.0]])]});
            var Q33;
            Q33=makeQuery(id+"F2.imprint","IMPRINT",FACE,{"disambiguationData":[TD([[makeQuery(id+"F2.imprint","IMPRINT",EDGE,{"derivedFrom":sQuery(id+"F2.wireOp",EDGE,"2cfb1138-f32f-4ed4-9923-472279ab65f4")}),1.0]])]});
            var Q34;
            Q34=makeQuery(id+"F2.imprint","IMPRINT",FACE,{"disambiguationData":[TD([[makeQuery(id+"F2.imprint","IMPRINT",EDGE,{"derivedFrom":sQuery(id+"F2.wireOp",EDGE,"cb2b1f7e-f635-4efb-b12c-495075b4995b")}),1.0]])]});
            var Q35;
            Q35=makeQuery(id+"F2.imprint","IMPRINT",FACE,{"disambiguationData":[TD([[makeQuery(id+"F2.imprint","IMPRINT",EDGE,{"derivedFrom":sQuery(id+"F2.wireOp",EDGE,"fe9d17d4-f2a5-44d9-8164-3530e82dfe4b")}),1.0]])]});
            var Q36;
            Q36=makeQuery(id+"F2.imprint","IMPRINT",FACE,{"disambiguationData":[TD([[makeQuery(id+"F2.imprint","IMPRINT",EDGE,{"derivedFrom":sQuery(id+"F2.wireOp",EDGE,"E66")}),-1.0]])]});
            var Q37;
            Q37=makeQuery(id+"F2.imprint","IMPRINT",FACE,{"disambiguationData":[TD([[makeQuery(id+"F2.imprint","IMPRINT",EDGE,{"derivedFrom":sQuery(id+"F2.wireOp",EDGE,"E4")}),-1.0]])]});
            var Q38;
            {var subQ0=sQuery(id+"F2.wireOp",EDGE,"E127");Q38=makeQuery(id+"F2.imprint","IMPRINT",FACE,{"disambiguationData":[TD([[makeQuery(id+"F2.imprint","IMPRINT",EDGE,{"derivedFrom":subQ0}),-1.0]])]});}
            var Q39;
            Q39=makeQuery(id+"F2.imprint","IMPRINT",FACE,{"disambiguationData":[TD([[makeQuery(id+"F2.imprint","IMPRINT",EDGE,{"derivedFrom":sQuery(id+"F2.wireOp",EDGE,"E59")}),-1.0]])]});
            var Q40;
            Q40=makeQuery(id+"F2.imprint","IMPRINT",FACE,{"disambiguationData":[TD([[makeQuery(id+"F2.imprint","IMPRINT",EDGE,{"derivedFrom":sQuery(id+"F2.wireOp",EDGE,"E57")}),-1.0]])]});
            var Q41;
            Q41=makeQuery(id+"F2.imprint","IMPRINT",FACE,{"disambiguationData":[TD([[makeQuery(id+"F2.imprint","IMPRINT",EDGE,{"derivedFrom":sQuery(id+"F2.wireOp",EDGE,"E53")}),-1.0]])]});
            var Q42;
            Q42=makeQuery(id+"F2.imprint","IMPRINT",FACE,{"disambiguationData":[TD([[makeQuery(id+"F2.imprint","IMPRINT",EDGE,{"derivedFrom":sQuery(id+"F2.wireOp",EDGE,"E5")}),1.0]])]});
            var Q43;
            Q43=makeQuery(id+"F2.imprint","IMPRINT",FACE,{"disambiguationData":[TD([[makeQuery(id+"F2.imprint","IMPRINT",EDGE,{"derivedFrom":sQuery(id+"F2.wireOp",EDGE,"E9")}),1.0]])]});
            var Q44;
            Q44=makeQuery(id+"F2.imprint","IMPRINT",FACE,{"disambiguationData":[TD([[makeQuery(id+"F2.imprint","IMPRINT",EDGE,{"derivedFrom":sQuery(id+"F2.wireOp",EDGE,"E49")}),1.0]])]});
            var Q45;
            Q45=makeQuery(id+"F2.imprint","IMPRINT",FACE,{"disambiguationData":[TD([[makeQuery(id+"F2.imprint","IMPRINT",EDGE,{"derivedFrom":sQuery(id+"F2.wireOp",EDGE,"E45")}),1.0]])]});
            var Q46;
            Q46=makeQuery(id+"F2.imprint","IMPRINT",FACE,{"disambiguationData":[TD([[makeQuery(id+"F2.imprint","IMPRINT",EDGE,{"derivedFrom":sQuery(id+"F2.wireOp",EDGE,"E13")}),1.0]])]});
            var Q47;
            Q47=makeQuery(id+"F2.imprint","IMPRINT",FACE,{"disambiguationData":[TD([[makeQuery(id+"F2.imprint","IMPRINT",EDGE,{"derivedFrom":sQuery(id+"F2.wireOp",EDGE,"E17")}),1.0]])]});
            var Q48;
            Q48=makeQuery(id+"F2.imprint","IMPRINT",FACE,{"disambiguationData":[TD([[makeQuery(id+"F2.imprint","IMPRINT",EDGE,{"derivedFrom":sQuery(id+"F2.wireOp",EDGE,"E41")}),1.0]])]});
            var Q49;
            Q49=makeQuery(id+"F2.imprint","IMPRINT",FACE,{"disambiguationData":[TD([[makeQuery(id+"F2.imprint","IMPRINT",EDGE,{"derivedFrom":sQuery(id+"F2.wireOp",EDGE,"E37")}),1.0]])]});
            var Q50;
            Q50=makeQuery(id+"F2.imprint","IMPRINT",FACE,{"disambiguationData":[TD([[makeQuery(id+"F2.imprint","IMPRINT",EDGE,{"derivedFrom":sQuery(id+"F2.wireOp",EDGE,"E21")}),1.0]])]});
            var Q51;
            Q51=makeQuery(id+"F2.imprint","IMPRINT",FACE,{"disambiguationData":[TD([[makeQuery(id+"F2.imprint","IMPRINT",EDGE,{"derivedFrom":sQuery(id+"F2.wireOp",EDGE,"E25")}),1.0]])]});
            var Q52;
            Q52=makeQuery(id+"F2.imprint","IMPRINT",FACE,{"disambiguationData":[TD([[makeQuery(id+"F2.imprint","IMPRINT",EDGE,{"derivedFrom":sQuery(id+"F2.wireOp",EDGE,"E33")}),1.0]])]});
            var Q53;
            Q53=makeQuery(id+"F2.imprint","IMPRINT",FACE,{"disambiguationData":[TD([[makeQuery(id+"F2.imprint","IMPRINT",EDGE,{"derivedFrom":sQuery(id+"F2.wireOp",EDGE,"E31")}),1.0]])]});
            var Q54;
            Q54=makeQuery(id+"F2.imprint","IMPRINT",FACE,{"disambiguationData":[TD([[makeQuery(id+"F2.imprint","IMPRINT",EDGE,{"derivedFrom":sQuery(id+"F2.wireOp",EDGE,"E29")}),1.0]])]});
            var Q55;
            Q55=makeQuery(id+"F2.imprint","IMPRINT",FACE,{"disambiguationData":[TD([[makeQuery(id+"F2.imprint","IMPRINT",EDGE,{"derivedFrom":sQuery(id+"F2.wireOp",EDGE,"E91")}),1.0]])]});
            var Q56;
            Q56=makeQuery(id+"F2.imprint","IMPRINT",FACE,{"disambiguationData":[TD([[makeQuery(id+"F2.imprint","IMPRINT",EDGE,{"derivedFrom":sQuery(id+"F2.wireOp",EDGE,"E93")}),1.0]])]});
            var Q57;
            Q57=makeQuery(id+"F2.imprint","IMPRINT",FACE,{"disambiguationData":[TD([[makeQuery(id+"F2.imprint","IMPRINT",EDGE,{"derivedFrom":sQuery(id+"F2.wireOp",EDGE,"E95")}),1.0]])]});
            var Q58;
            Q58=makeQuery(id+"F2.imprint","IMPRINT",FACE,{"disambiguationData":[TD([[makeQuery(id+"F2.imprint","IMPRINT",EDGE,{"derivedFrom":sQuery(id+"F2.wireOp",EDGE,"E87")}),1.0]])]});
            var Q59;
            Q59=makeQuery(id+"F2.imprint","IMPRINT",FACE,{"disambiguationData":[TD([[makeQuery(id+"F2.imprint","IMPRINT",EDGE,{"derivedFrom":sQuery(id+"F2.wireOp",EDGE,"E83")}),1.0]])]});
            var Q60;
            Q60=makeQuery(id+"F2.imprint","IMPRINT",FACE,{"disambiguationData":[TD([[makeQuery(id+"F2.imprint","IMPRINT",EDGE,{"derivedFrom":sQuery(id+"F2.wireOp",EDGE,"E99")}),1.0]])]});
            var Q61;
            Q61=makeQuery(id+"F2.imprint","IMPRINT",FACE,{"disambiguationData":[TD([[makeQuery(id+"F2.imprint","IMPRINT",EDGE,{"derivedFrom":sQuery(id+"F2.wireOp",EDGE,"E103")}),1.0]])]});
            var Q62;
            Q62=makeQuery(id+"F2.imprint","IMPRINT",FACE,{"disambiguationData":[TD([[makeQuery(id+"F2.imprint","IMPRINT",EDGE,{"derivedFrom":sQuery(id+"F2.wireOp",EDGE,"E79")}),1.0]])]});
            var Q63;
            Q63=makeQuery(id+"F2.imprint","IMPRINT",FACE,{"disambiguationData":[TD([[makeQuery(id+"F2.imprint","IMPRINT",EDGE,{"derivedFrom":sQuery(id+"F2.wireOp",EDGE,"E75")}),1.0]])]});
            var Q64;
            Q64=makeQuery(id+"F2.imprint","IMPRINT",FACE,{"disambiguationData":[TD([[makeQuery(id+"F2.imprint","IMPRINT",EDGE,{"derivedFrom":sQuery(id+"F2.wireOp",EDGE,"E107")}),1.0]])]});
            var Q65;
            Q65=makeQuery(id+"F2.imprint","IMPRINT",FACE,{"disambiguationData":[TD([[makeQuery(id+"F2.imprint","IMPRINT",EDGE,{"derivedFrom":sQuery(id+"F2.wireOp",EDGE,"E111")}),1.0]])]});
            var Q66;
            Q66=makeQuery(id+"F2.imprint","IMPRINT",FACE,{"disambiguationData":[TD([[makeQuery(id+"F2.imprint","IMPRINT",EDGE,{"derivedFrom":sQuery(id+"F2.wireOp",EDGE,"E71")}),1.0]])]});
            var Q67;
            Q67=makeQuery(id+"F2.imprint","IMPRINT",FACE,{"disambiguationData":[TD([[makeQuery(id+"F2.imprint","IMPRINT",EDGE,{"derivedFrom":sQuery(id+"F2.wireOp",EDGE,"E67")}),1.0]])]});
            var Q68;
            Q68=makeQuery(id+"F2.imprint","IMPRINT",FACE,{"disambiguationData":[TD([[makeQuery(id+"F2.imprint","IMPRINT",EDGE,{"derivedFrom":sQuery(id+"F2.wireOp",EDGE,"E115")}),-1.0]])]});
            var Q69;
            Q69=makeQuery(id+"F2.imprint","IMPRINT",FACE,{"disambiguationData":[TD([[makeQuery(id+"F2.imprint","IMPRINT",EDGE,{"derivedFrom":sQuery(id+"F2.wireOp",EDGE,"E119")}),-1.0]])]});
            var Q70;
            Q70=makeQuery(id+"F2.imprint","IMPRINT",FACE,{"disambiguationData":[TD([[makeQuery(id+"F2.imprint","IMPRINT",EDGE,{"derivedFrom":sQuery(id+"F2.wireOp",EDGE,"E121")}),-1.0]])]});
            extrude(context, id + "F3", {"entities" : qUnion([Q0, Q1, Q2, Q3, Q4, Q5, Q6, Q7, Q8, Q9, Q10, Q11, Q12, Q13, Q14, Q15, Q16, Q17, Q18, Q19, Q20, Q21, Q22, Q23, Q24, Q25, Q26, Q27, Q28, Q29, Q30, Q31, Q32, Q33, Q34, Q35, Q36, Q37, Q38, Q39, Q40, Q41, Q42, Q43, Q44, Q45, Q46, Q47, Q48, Q49, Q50, Q51, Q52, Q53, Q54, Q55, Q56, Q57, Q58, Q59, Q60, Q61, Q62, Q63, Q64, Q65, Q66, Q67, Q68, Q69, Q70]), "operationType" : NewBodyOperationType.ADD, "depth" : 0.8 * mm});
        }
        {
            var Q0;
            Q0=makeQuery(id+"F3.boolean.opBoolean","SPLIT",FACE,{"disambiguationData":[TD([makeQuery(id+"F3.opExtrude","SWEPT_FACE",FACE,{"disambiguationData":[OSD([sQuery(id+"F2.wireOp",EDGE,"E1")])]})])],"derivedFrom":makeQuery(id+"F1.opExtrude","CAP_FACE",FACE,{"disambiguationData":[OSD([sQuery(id+"F0.wireOp",EDGE,"E0")])],"isStart":false})});
            var sketch = newSketch(context, id + "F4", { "sketchPlane" : qUnion([Q0])});
            skEllipse(sketch, "E133", {"center": v(0, 0) * mm, "majorRadius": 1.9 * mm, "minorRadius": 0.64 * mm, "majorAxis": v(0, 1)});
            skPoint(sketch, "E134.end.orphan", {"position": v(0, 1.9) * mm});
            skPoint(sketch, "E135.end.orphan", {"position": v(0.64, 0) * mm});
            skPoint(sketch, "E136.end.orphan", {"position": v(0, -1.9) * mm});
            skPoint(sketch, "E136.start.orphan", {"position": v(-0.64, 0) * mm});
            skSolve(sketch);
        }
        {
            var Q0;
            Q0 = qSketchRegion(id + "F4", true);
            extrude(context, id + "F5", {"entities" : qUnion([Q0]), "operationType" : NewBodyOperationType.ADD, "depth" : 12.7 * mm});
        }
        {
            var Q0;
            Q0=qCreatedBy(makeId("Right.planeOp"),FACE);
            var sketch = newSketch(context, id + "F6", { "sketchPlane" : qUnion([Q0])});
            skArc(sketch, "E137", {"start": v(3.8, 13.97) * mm, "mid": v(0, 13.68) * mm, "end": v(-3.8, 13.97) * mm});
            skArc(sketch, "E138.0", {"start": v(3.43, 16.48) * mm, "mid": v(0, 16.22) * mm, "end": v(-3.43, 16.48) * mm});
            skLineSegment(sketch, "E139", {"start": v(3.8, 13.97) * mm, "end": v(3.43, 16.48) * mm});
            skLineSegment(sketch, "E140", {"start": v(-3.43, 16.48) * mm, "end": v(-3.8, 13.97) * mm});
            skSolve(sketch);
        }
        {
            var Q0;
            Q0 = qSketchRegion(id + "F6", true);
            extrude(context, id + "F7", {"entities" : qUnion([Q0]), "operationType" : NewBodyOperationType.ADD, "endBound" : BoundingType.SYMMETRIC, "depth" : 1.52 * mm});
        }
        {
            var Q0;
            Q0=qCreatedBy(makeId("Right.planeOp"),FACE);
            var sketch = newSketch(context, id + "F8", { "sketchPlane" : qUnion([Q0])});
            skLineSegment(sketch, "E141", {"start": v(0, 13.97) * mm, "end": v(0, 21.6) * mm});
            skLineSegment(sketch, "E142", {"start": v(0, 21.6) * mm, "end": v(0.76, 21.6) * mm});
            skLineSegment(sketch, "E143", {"start": v(0.76, 21.6) * mm, "end": v(0.76, 13.97) * mm});
            skLineSegment(sketch, "E144", {"start": v(0.76, 13.97) * mm, "end": v(0, 13.97) * mm});
            skSolve(sketch);
        }
        {
            var Q0;
            Q0 = qSketchRegion(id + "F8", true);
            var Q1;
            Q1=sQuery(id+"F8.wireOp",EDGE,"E141");
            revolve(context, id + "F9", {"operationType" : NewBodyOperationType.ADD, "entities" : qUnion([Q0]), "axis" : qUnion([Q1]), "revolveType" : RevolveType.FULL});
        }
        {
            var Q0;
            Q0=makeQuery(id+"F9.opRevolve","SWEPT_FACE",FACE,{"disambiguationData":[OSD([sQuery(id+"F8.wireOp",EDGE,"E142")])]});
            var sketch = newSketch(context, id + "F10", { "sketchPlane" : qUnion([Q0])});
            skCircle(sketch, "E145.cCircle", {"center": v(0, 0) * mm, "radius": 1.27 * mm, "construction": true});
            skLineSegment(sketch, "E145.0", {"start": v(0.53, -1.27) * mm, "end": v(-0.53, -1.27) * mm});
            skLineSegment(sketch, "E145.1", {"start": v(-0.53, -1.27) * mm, "end": v(-1.27, -0.53) * mm});
            skLineSegment(sketch, "E145.2", {"start": v(-1.27, -0.53) * mm, "end": v(-1.27, 0.53) * mm});
            skLineSegment(sketch, "E145.3", {"start": v(-1.27, 0.53) * mm, "end": v(-0.53, 1.27) * mm});
            skLineSegment(sketch, "E145.4", {"start": v(-0.53, 1.27) * mm, "end": v(0.53, 1.27) * mm});
            skLineSegment(sketch, "E145.5", {"start": v(0.53, 1.27) * mm, "end": v(1.27, 0.53) * mm});
            skLineSegment(sketch, "E145.6", {"start": v(1.27, 0.53) * mm, "end": v(1.27, -0.53) * mm});
            skLineSegment(sketch, "E145.7", {"start": v(1.27, -0.53) * mm, "end": v(0.53, -1.27) * mm});
            skPoint(sketch, "E145.0.midPoint", {"position": v(0, -1.27) * mm});
            skSolve(sketch);
        }
        {
            var Q0;
            Q0 = qSketchRegion(id + "F10", true);
            extrude(context, id + "F11", {"entities" : qUnion([Q0]), "operationType" : NewBodyOperationType.ADD, "depth" : 2.54 * mm});
        }
        {
            var Q0;
            Q0=makeQuery(id+"F11.opExtrude","SWEPT_FACE",FACE,{"disambiguationData":[OSD([sQuery(id+"F10.wireOp",EDGE,"E145.6")])]});
            var sketch = newSketch(context, id + "F12", { "sketchPlane" : qUnion([Q0])});
            skCircle(sketch, "E146.cCircle", {"center": v(0, 22.86) * mm, "radius": 1.27 * mm, "construction": true});
            skLineSegment(sketch, "E146.0", {"start": v(-0.53, 24.13) * mm, "end": v(0.53, 24.13) * mm});
            skLineSegment(sketch, "E146.1", {"start": v(0.53, 24.13) * mm, "end": v(1.27, 23.39) * mm});
            skLineSegment(sketch, "E146.2", {"start": v(1.27, 23.39) * mm, "end": v(1.27, 22.33) * mm});
            skLineSegment(sketch, "E146.3", {"start": v(1.27, 22.33) * mm, "end": v(0.53, 21.6) * mm});
            skLineSegment(sketch, "E146.4", {"start": v(0.53, 21.6) * mm, "end": v(-0.53, 21.6) * mm});
            skLineSegment(sketch, "E146.5", {"start": v(-0.53, 21.6) * mm, "end": v(-1.27, 22.33) * mm});
            skLineSegment(sketch, "E146.6", {"start": v(-1.27, 22.33) * mm, "end": v(-1.27, 23.39) * mm});
            skLineSegment(sketch, "E146.7", {"start": v(-1.27, 23.39) * mm, "end": v(-0.53, 24.13) * mm});
            skPoint(sketch, "E146.0.midPoint", {"position": v(0, 24.13) * mm});
            skLineSegment(sketch, "E147.bottom", {"start": v(-1.27, 21.6) * mm, "end": v(1.27, 21.6) * mm});
            skLineSegment(sketch, "E147.top", {"start": v(-1.27, 24.13) * mm, "end": v(1.27, 24.13) * mm});
            skLineSegment(sketch, "E147.left", {"start": v(-1.27, 21.6) * mm, "end": v(-1.27, 24.13) * mm});
            skLineSegment(sketch, "E147.right", {"start": v(1.27, 21.6) * mm, "end": v(1.27, 24.13) * mm});
            skSolve(sketch);
        }
        {
            var Q0;
            {var subQ0=sQuery(id+"F12.wireOp",EDGE,"E146.3");Q0=makeQuery(id+"F12.imprint","IMPRINT",FACE,{"disambiguationData":[TD([[makeQuery(id+"F12.imprint","IMPRINT",EDGE,{"derivedFrom":subQ0}),1.0]])]});}
            var Q1;
            {var subQ0=sQuery(id+"F12.wireOp",EDGE,"E146.5");Q1=makeQuery(id+"F12.imprint","IMPRINT",FACE,{"disambiguationData":[TD([[makeQuery(id+"F12.imprint","IMPRINT",EDGE,{"derivedFrom":subQ0}),1.0]])]});}
            var Q2;
            {var subQ0=sQuery(id+"F12.wireOp",EDGE,"E146.7");Q2=makeQuery(id+"F12.imprint","IMPRINT",FACE,{"disambiguationData":[TD([[makeQuery(id+"F12.imprint","IMPRINT",EDGE,{"derivedFrom":subQ0}),1.0]])]});}
            var Q3;
            {var subQ0=sQuery(id+"F12.wireOp",EDGE,"E146.1");Q3=makeQuery(id+"F12.imprint","IMPRINT",FACE,{"disambiguationData":[TD([[makeQuery(id+"F12.imprint","IMPRINT",EDGE,{"derivedFrom":subQ0}),1.0]])]});}
            extrude(context, id + "F13", {"entities" : qUnion([Q0, Q1, Q2, Q3]), "operationType" : NewBodyOperationType.REMOVE, "oppositeDirection" : true, "depth" : 25.4 * mm});
        }
        {
            var Q0;
            Q0=makeQuery(id+"F11.opExtrude","SWEPT_FACE",FACE,{"disambiguationData":[OSD([sQuery(id+"F10.wireOp",EDGE,"E145.0")])]});
            var sketch = newSketch(context, id + "F14", { "sketchPlane" : qUnion([Q0])});
            skCircle(sketch, "E148.cCircle", {"center": v(0, 22.86) * mm, "radius": 1.27 * mm, "construction": true});
            skPoint(sketch, "E148.cCircle.centerSnap0", {"position": v(0.53, 22.86) * mm});
            skLineSegment(sketch, "E148.0", {"start": v(1.27, 23.39) * mm, "end": v(1.27, 22.33) * mm});
            skLineSegment(sketch, "E148.1", {"start": v(1.27, 22.33) * mm, "end": v(0.53, 21.6) * mm});
            skLineSegment(sketch, "E148.2", {"start": v(0.53, 21.6) * mm, "end": v(-0.53, 21.6) * mm});
            skLineSegment(sketch, "E148.3", {"start": v(-0.53, 21.6) * mm, "end": v(-1.27, 22.33) * mm});
            skLineSegment(sketch, "E148.4", {"start": v(-1.27, 22.33) * mm, "end": v(-1.27, 23.39) * mm});
            skLineSegment(sketch, "E148.5", {"start": v(-1.27, 23.39) * mm, "end": v(-0.53, 24.13) * mm});
            skLineSegment(sketch, "E148.6", {"start": v(-0.53, 24.13) * mm, "end": v(0.53, 24.13) * mm});
            skLineSegment(sketch, "E148.7", {"start": v(0.53, 24.13) * mm, "end": v(1.27, 23.39) * mm});
            skPoint(sketch, "E148.0.midPoint", {"position": v(1.27, 22.86) * mm});
            skLineSegment(sketch, "E149.bottom", {"start": v(-1.27, 21.6) * mm, "end": v(1.27, 21.6) * mm});
            skLineSegment(sketch, "E149.top", {"start": v(-1.27, 24.13) * mm, "end": v(1.27, 24.13) * mm});
            skLineSegment(sketch, "E149.left", {"start": v(-1.27, 21.6) * mm, "end": v(-1.27, 24.13) * mm});
            skLineSegment(sketch, "E149.right", {"start": v(1.27, 21.6) * mm, "end": v(1.27, 24.13) * mm});
            skSolve(sketch);
        }
        {
            var Q0;
            {var subQ0=sQuery(id+"F14.wireOp",EDGE,"E148.1");Q0=makeQuery(id+"F14.imprint","IMPRINT",FACE,{"disambiguationData":[TD([[makeQuery(id+"F14.imprint","IMPRINT",EDGE,{"derivedFrom":subQ0}),1.0]])]});}
            var Q1;
            {var subQ0=sQuery(id+"F14.wireOp",EDGE,"E148.3");Q1=makeQuery(id+"F14.imprint","IMPRINT",FACE,{"disambiguationData":[TD([[makeQuery(id+"F14.imprint","IMPRINT",EDGE,{"derivedFrom":subQ0}),1.0]])]});}
            var Q2;
            {var subQ0=sQuery(id+"F14.wireOp",EDGE,"E148.5");Q2=makeQuery(id+"F14.imprint","IMPRINT",FACE,{"disambiguationData":[TD([[makeQuery(id+"F14.imprint","IMPRINT",EDGE,{"derivedFrom":subQ0}),1.0]])]});}
            var Q3;
            {var subQ0=sQuery(id+"F14.wireOp",EDGE,"E148.7");Q3=makeQuery(id+"F14.imprint","IMPRINT",FACE,{"disambiguationData":[TD([[makeQuery(id+"F14.imprint","IMPRINT",EDGE,{"derivedFrom":subQ0}),1.0]])]});}
            extrude(context, id + "F15", {"entities" : qUnion([Q0, Q1, Q2, Q3]), "operationType" : NewBodyOperationType.REMOVE, "endBound" : BoundingType.THROUGH_ALL, "oppositeDirection" : true, "depth" : 25.4 * mm});
        }
    });
